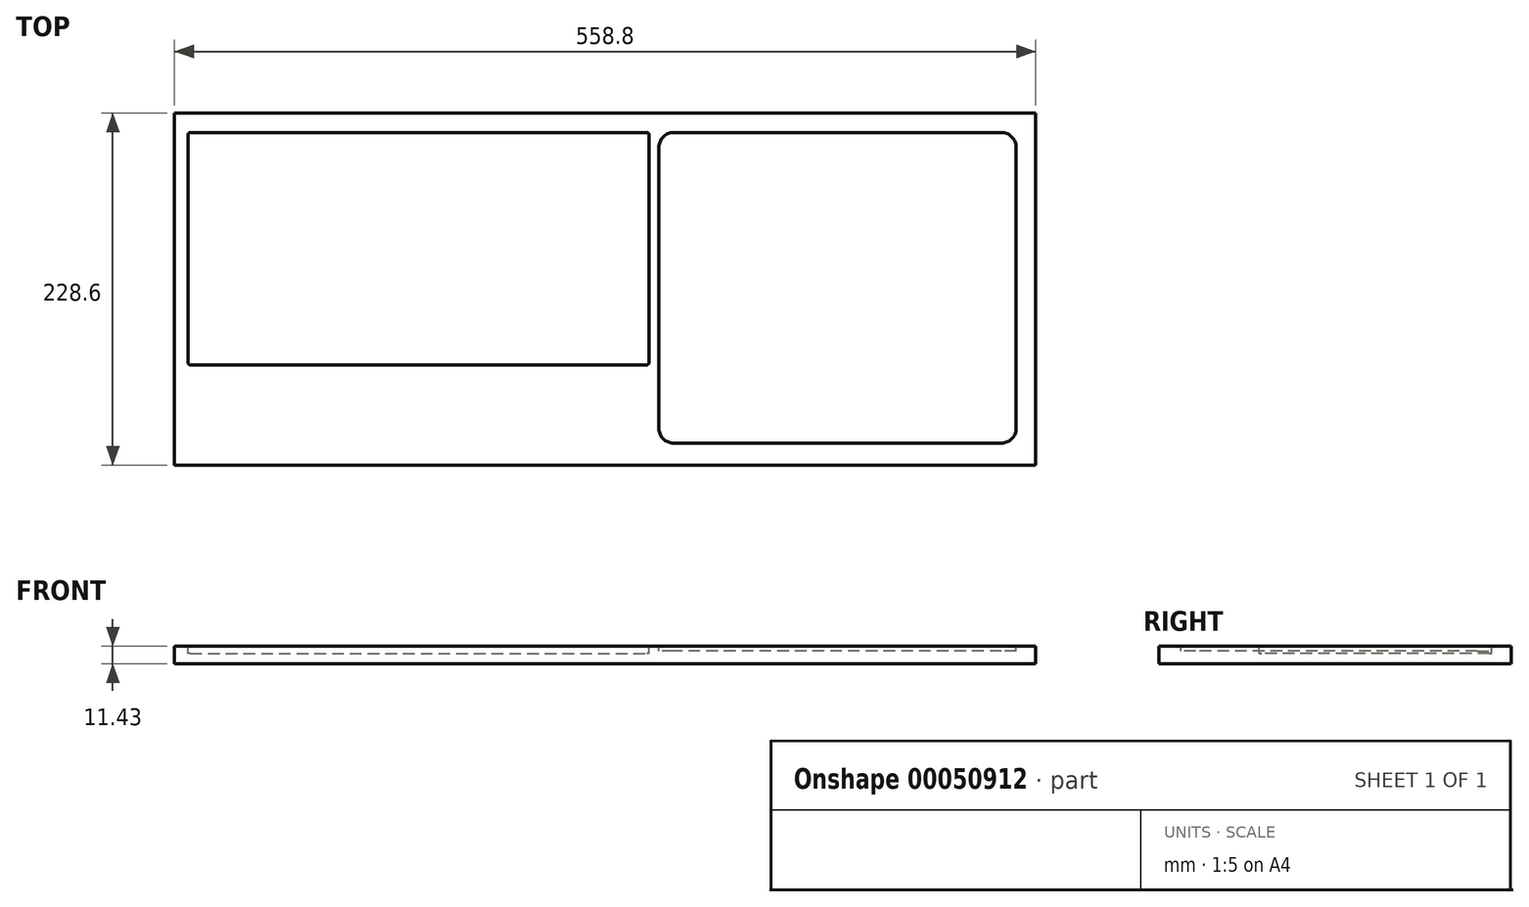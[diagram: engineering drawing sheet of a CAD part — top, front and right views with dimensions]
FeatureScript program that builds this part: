
annotation { "Feature Type Name" : "Feature", "Feature Type Description" : "" }
export const myFeature = defineFeature(function(context is Context, id is Id, definition is map)
    precondition{}
    {
        {
            var Q0;
            Q0=qCreatedBy(makeId("Top.planeOp"),FACE);
            var sketch = newSketch(context, id + "F0", { "sketchPlane" : qUnion([Q0])});
            skLineSegment(sketch, "E0.rect.bottom", {"start": v(106.36, 100.8) * mm, "end": v(-106.36, 100.8) * mm});
            skLineSegment(sketch, "E0.rect.top", {"start": v(106.36, -100.8) * mm, "end": v(-106.36, -100.8) * mm});
            skLineSegment(sketch, "E0.rect.left", {"start": v(115.89, 91.28) * mm, "end": v(115.89, -91.28) * mm});
            skLineSegment(sketch, "E0.rect.right", {"start": v(-115.89, 91.28) * mm, "end": v(-115.89, -91.28) * mm});
            skPoint(sketch, "E0.rect.middle", {"position": v(0, 0) * mm});
            skPoint(sketch, "E1.visualSharp", {"position": v(-115.89, 100.8) * mm});
            skArc(sketch, "E1.filletArc", {"start": v(-106.36, 100.8) * mm, "mid": v(-113.1, 98.02) * mm, "end": v(-115.89, 91.28) * mm});
            skPoint(sketch, "E2.visualSharp", {"position": v(115.89, 100.8) * mm});
            skArc(sketch, "E2.filletArc", {"start": v(115.89, 91.28) * mm, "mid": v(113.1, 98.02) * mm, "end": v(106.36, 100.8) * mm});
            skPoint(sketch, "E3.visualSharp", {"position": v(115.89, -100.8) * mm});
            skArc(sketch, "E3.filletArc", {"start": v(106.36, -100.8) * mm, "mid": v(113.1, -98.02) * mm, "end": v(115.89, -91.28) * mm});
            skPoint(sketch, "E4.visualSharp", {"position": v(-115.89, -100.8) * mm});
            skArc(sketch, "E4.filletArc", {"start": v(-115.89, -91.28) * mm, "mid": v(-113.1, -98.02) * mm, "end": v(-106.36, -100.8) * mm});
            skLineSegment(sketch, "E5.bottom", {"start": v(-430.21, 113.5) * mm, "end": v(128.59, 113.5) * mm});
            skLineSegment(sketch, "E5.top", {"start": v(-430.21, -115.1) * mm, "end": v(128.59, -115.1) * mm});
            skLineSegment(sketch, "E5.left", {"start": v(-430.21, 113.5) * mm, "end": v(-430.21, -115.1) * mm});
            skLineSegment(sketch, "E5.right", {"start": v(128.59, 113.5) * mm, "end": v(128.59, -115.1) * mm});
            skLineSegment(sketch, "E6.bottom", {"start": v(-419.9, 100.8) * mm, "end": v(-123.83, 100.8) * mm});
            skLineSegment(sketch, "E6.top", {"start": v(-419.9, -50) * mm, "end": v(-123.83, -50) * mm});
            skLineSegment(sketch, "E6.left", {"start": v(-421.48, 99.22) * mm, "end": v(-421.48, -48.42) * mm});
            skLineSegment(sketch, "E6.right", {"start": v(-122.24, 99.22) * mm, "end": v(-122.24, -48.42) * mm});
            skPoint(sketch, "E7.visualSharp", {"position": v(-421.48, 100.8) * mm});
            skArc(sketch, "E7.filletArc", {"start": v(-419.9, 100.8) * mm, "mid": v(-421.02, 100.34) * mm, "end": v(-421.48, 99.22) * mm});
            skPoint(sketch, "E8.visualSharp", {"position": v(-122.24, 100.8) * mm});
            skArc(sketch, "E8.filletArc", {"start": v(-122.24, 99.22) * mm, "mid": v(-122.7, 100.34) * mm, "end": v(-123.83, 100.8) * mm});
            skPoint(sketch, "E9.visualSharp", {"position": v(-122.24, -50) * mm});
            skArc(sketch, "E9.filletArc", {"start": v(-123.83, -50) * mm, "mid": v(-122.7, -49.54) * mm, "end": v(-122.24, -48.42) * mm});
            skPoint(sketch, "E10.visualSharp", {"position": v(-421.48, -50) * mm});
            skArc(sketch, "E10.filletArc", {"start": v(-421.48, -48.42) * mm, "mid": v(-421.02, -49.54) * mm, "end": v(-419.9, -50) * mm});
            skSolve(sketch);
        }
        {
            var Q0;
            Q0=makeQuery(id+"F0.imprint","IMPRINT",FACE,{"disambiguationData":[TD([[makeQuery(id+"F0.imprint","IMPRINT",EDGE,{"derivedFrom":sQuery(id+"F0.wireOp",EDGE,"E0.rect.bottom")}),-1.0]])]});
            var Q1;
            Q1=makeQuery(id+"F0.imprint","IMPRINT",FACE,{"disambiguationData":[TD([[makeQuery(id+"F0.imprint","IMPRINT",EDGE,{"derivedFrom":sQuery(id+"F0.wireOp",EDGE,"E6.bottom")}),-1.0]])]});
            var Q2;
            Q2=makeQuery(id+"F0.imprint","IMPRINT",FACE,{"disambiguationData":[TD([[makeQuery(id+"F0.imprint","IMPRINT",EDGE,{"derivedFrom":sQuery(id+"F0.wireOp",EDGE,"E0.rect.bottom")}),1.0]])]});
            extrude(context, id + "F1", {"entities" : qUnion([Q0, Q1, Q2]), "oppositeDirection" : true, "depth" : 11.43 * mm});
        }
        {
            var Q0;
            Q0=makeQuery(id+"F0.imprint","IMPRINT",FACE,{"disambiguationData":[TD([[makeQuery(id+"F0.imprint","IMPRINT",EDGE,{"derivedFrom":sQuery(id+"F0.wireOp",EDGE,"E6.bottom")}),-1.0]])]});
            extrude(context, id + "F2", {"entities" : qUnion([Q0]), "operationType" : NewBodyOperationType.REMOVE, "oppositeDirection" : true, "depth" : 4.76 * mm});
        }
        {
            var Q0;
            Q0=makeQuery(id+"F0.imprint","IMPRINT",FACE,{"disambiguationData":[TD([[makeQuery(id+"F0.imprint","IMPRINT",EDGE,{"derivedFrom":sQuery(id+"F0.wireOp",EDGE,"E0.rect.bottom")}),1.0]])]});
            extrude(context, id + "F3", {"entities" : qUnion([Q0]), "operationType" : NewBodyOperationType.REMOVE, "oppositeDirection" : true, "depth" : 3.17 * mm});
        }
    });
